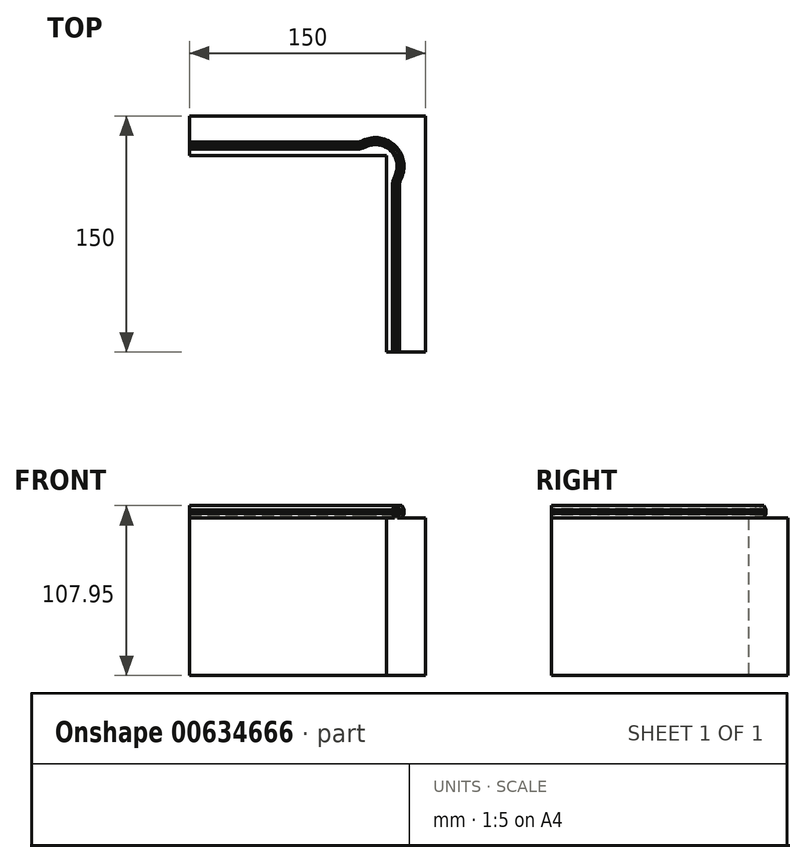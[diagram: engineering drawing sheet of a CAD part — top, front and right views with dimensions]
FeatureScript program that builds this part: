
annotation { "Feature Type Name" : "Feature", "Feature Type Description" : "" }
export const myFeature = defineFeature(function(context is Context, id is Id, definition is map)
    precondition{}
    {
        {
            var Q0;
            Q0=qCreatedBy(makeId("Top.planeOp"),FACE);
            var sketch = newSketch(context, id + "F0", { "sketchPlane" : qUnion([Q0])});
            skLineSegment(sketch, "E0", {"start": v(0, 0) * mm, "end": v(0, -150) * mm});
            skLineSegment(sketch, "E1", {"start": v(0, -150) * mm, "end": v(-25, -150) * mm});
            skLineSegment(sketch, "E2", {"start": v(-25, -150) * mm, "end": v(-25, -25) * mm});
            skLineSegment(sketch, "E3", {"start": v(-25, -25) * mm, "end": v(-150, -25) * mm});
            skLineSegment(sketch, "E4", {"start": v(-150, -25) * mm, "end": v(-150, 0) * mm});
            skLineSegment(sketch, "E5", {"start": v(-150, 0) * mm, "end": v(0, 0) * mm});
            skSolve(sketch);
        }
        {
            var Q0;
            Q0 = qSketchRegion(id + "F0", true);
            extrude(context, id + "F1", {"entities" : qUnion([Q0]), "depth" : 100 * mm, "offsetDistance" : 25.4 * mm});
        }
        {
            var Q0;
            Q0=makeQuery(id+"F1.opExtrude","CAP_FACE",FACE,{"disambiguationData":[OSD([sQuery(id+"F0.wireOp",EDGE,"E0"),sQuery(id+"F0.wireOp",EDGE,"E1"),sQuery(id+"F0.wireOp",EDGE,"E2"),sQuery(id+"F0.wireOp",EDGE,"E3"),sQuery(id+"F0.wireOp",EDGE,"E4"),sQuery(id+"F0.wireOp",EDGE,"E5")])],"isStart":false});
            var sketch = newSketch(context, id + "F2", { "sketchPlane" : qUnion([Q0])});
            skLineSegment(sketch, "E6", {"start": v(-150, -18.9) * mm, "end": v(-44.4, -18.9) * mm});
            skLineSegment(sketch, "E7", {"start": v(-18.9, -150) * mm, "end": v(-18.9, -44.4) * mm});
            skLineSegment(sketch, "E8", {"start": v(-76.04, -18.9) * mm, "end": v(-76.04, -25) * mm, "construction": true});
            skLineSegment(sketch, "E9", {"start": v(-18.9, -125.71) * mm, "end": v(-25, -125.71) * mm, "construction": true});
            skArc(sketch, "E10", {"start": v(-44.4, -18.9) * mm, "mid": v(-41.68, -18.59) * mm, "end": v(-39.1, -17.66) * mm});
            skArc(sketch, "E11", {"start": v(-17.66, -39.1) * mm, "mid": v(-20.69, -20.69) * mm, "end": v(-39.1, -17.66) * mm});
            skArc(sketch, "E12", {"start": v(-17.66, -39.1) * mm, "mid": v(-18.59, -41.68) * mm, "end": v(-18.9, -44.4) * mm});
            skLineSegment(sketch, "E13", {"start": v(-20.69, -20.69) * mm, "end": v(-25, -25) * mm, "construction": true});
            skLineSegment(sketch, "E14", {"start": v(0, -45.02) * mm, "end": v(-10.97, -45.02) * mm});
            skLineSegment(sketch, "E15", {"start": v(-10.97, -45.02) * mm, "end": v(-10.97, -34.98) * mm});
            skLineSegment(sketch, "E16", {"start": v(-10.97, -34.98) * mm, "end": v(0, -34.98) * mm});
            skArc(sketch, "E17", {"start": v(-10.97, -34.98) * mm, "mid": v(-15.99, -40) * mm, "end": v(-10.97, -45.02) * mm});
            skSolve(sketch);
        }
        {
            var Q0;
            Q0=makeQuery(id+"F1.opExtrude","SWEPT_FACE",FACE,{"disambiguationData":[OSD([sQuery(id+"F0.wireOp",EDGE,"E4")])]});
            var sketch = newSketch(context, id + "F3", { "sketchPlane" : qUnion([Q0])});
            skLineSegment(sketch, "E18", {"start": v(18.07, 100) * mm, "end": v(19.73, 100) * mm});
            skLineSegment(sketch, "E19", {"start": v(19.73, 100) * mm, "end": v(21.1, 102.88) * mm});
            skLineSegment(sketch, "E20", {"start": v(21.1, 102.88) * mm, "end": v(21.1, 105.08) * mm});
            skLineSegment(sketch, "E21", {"start": v(21.1, 105.08) * mm, "end": v(19.73, 107.95) * mm});
            skLineSegment(sketch, "E22", {"start": v(19.73, 107.95) * mm, "end": v(18.07, 107.95) * mm});
            skLineSegment(sketch, "E23", {"start": v(18.07, 107.95) * mm, "end": v(16.7, 105.08) * mm});
            skLineSegment(sketch, "E24", {"start": v(16.7, 105.08) * mm, "end": v(16.7, 102.88) * mm});
            skLineSegment(sketch, "E25", {"start": v(16.7, 102.88) * mm, "end": v(18.07, 100) * mm});
            skLineSegment(sketch, "E26", {"start": v(18.07, 107.95) * mm, "end": v(18.07, 100) * mm, "construction": true});
            skLineSegment(sketch, "E27", {"start": v(16.7, 105.08) * mm, "end": v(21.1, 105.08) * mm, "construction": true});
            skLineSegment(sketch, "E28", {"start": v(18.9, 107.95) * mm, "end": v(18.9, 100) * mm, "construction": true});
            skLineSegment(sketch, "E29", {"start": v(18.23, 105.98) * mm, "end": v(19.57, 105.98) * mm});
            skLineSegment(sketch, "E30", {"start": v(19.57, 105.98) * mm, "end": v(20.05, 104.97) * mm});
            skLineSegment(sketch, "E31", {"start": v(20.05, 104.97) * mm, "end": v(20.05, 102.98) * mm});
            skLineSegment(sketch, "E32", {"start": v(20.05, 102.98) * mm, "end": v(19.57, 101.97) * mm});
            skLineSegment(sketch, "E33", {"start": v(19.57, 101.98) * mm, "end": v(18.23, 101.98) * mm});
            skLineSegment(sketch, "E34", {"start": v(18.23, 101.97) * mm, "end": v(17.75, 102.98) * mm});
            skLineSegment(sketch, "E35", {"start": v(17.75, 102.98) * mm, "end": v(17.75, 104.97) * mm});
            skLineSegment(sketch, "E36", {"start": v(17.75, 104.97) * mm, "end": v(18.23, 105.98) * mm});
            skLineSegment(sketch, "E37", {"start": v(17.75, 104.97) * mm, "end": v(20.05, 104.97) * mm, "construction": true});
            skLineSegment(sketch, "E38", {"start": v(16.7, 105.08) * mm, "end": v(17.75, 104.97) * mm, "construction": true});
            skLineSegment(sketch, "E39", {"start": v(17.75, 102.98) * mm, "end": v(16.7, 102.88) * mm, "construction": true});
            skLineSegment(sketch, "E40", {"start": v(20.05, 102.98) * mm, "end": v(21.1, 102.88) * mm, "construction": true});
            skLineSegment(sketch, "E41", {"start": v(20.05, 104.97) * mm, "end": v(21.1, 105.07) * mm, "construction": true});
            skLineSegment(sketch, "E42", {"start": v(18.23, 101.98) * mm, "end": v(18.23, 100) * mm, "construction": true});
            skLineSegment(sketch, "E43", {"start": v(18.23, 105.98) * mm, "end": v(18.23, 107.95) * mm, "construction": true});
            skSolve(sketch);
        }
        {
            var Q0;
            Q0=makeQuery(id+"F3.imprint","IMPRINT",FACE,{"disambiguationData":[TD([[makeQuery(id+"F3.imprint","IMPRINT",EDGE,{"derivedFrom":sQuery(id+"F3.wireOp",EDGE,"E18")}),-1.0]])]});
            var Q1;
            Q1=sQuery(id+"F2.wireOp",EDGE,"E6");
            var Q2;
            Q2=sQuery(id+"F2.wireOp",EDGE,"E11");
            var Q3;
            Q3=sQuery(id+"F2.wireOp",EDGE,"E10");
            var Q4;
            Q4=sQuery(id+"F2.wireOp",EDGE,"E12");
            var Q5;
            Q5=sQuery(id+"F2.wireOp",EDGE,"E7");
            sweep(context, id + "F4", {"operationType" : NewBodyOperationType.ADD, "profiles" : qUnion([Q0]), "path" : qUnion([Q1, Q2, Q3, Q4, Q5])});
        }
    });
